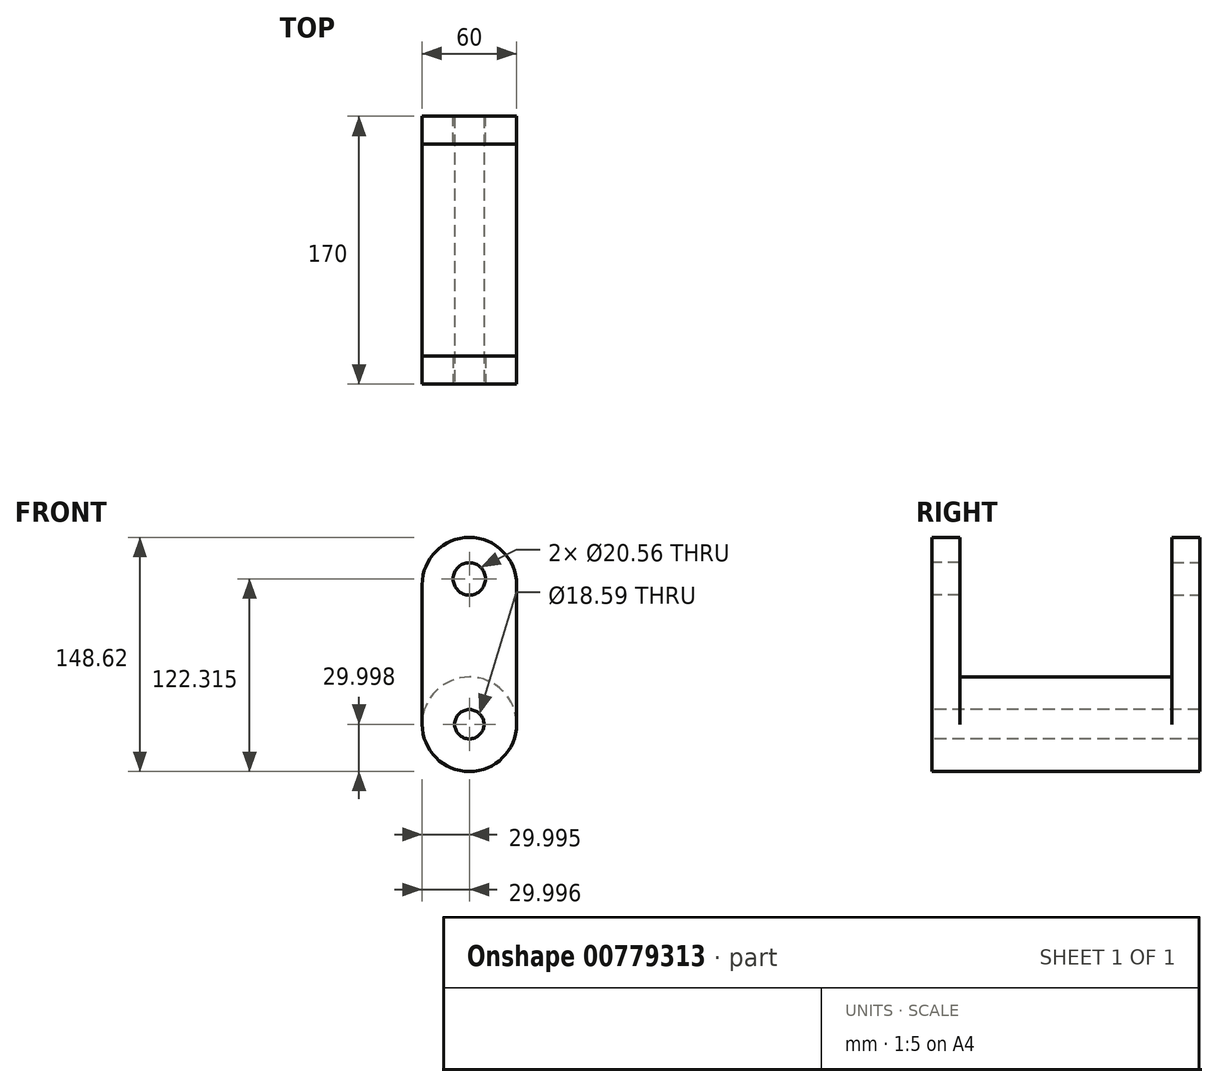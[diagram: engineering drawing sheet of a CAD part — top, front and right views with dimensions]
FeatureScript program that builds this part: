
annotation { "Feature Type Name" : "Feature", "Feature Type Description" : "" }
export const myFeature = defineFeature(function(context is Context, id is Id, definition is map)
    precondition{}
    {
        {
            var Q0;
            Q0=qCreatedBy(makeId("Front.planeOp"),FACE);
            var sketch = newSketch(context, id + "F0", { "sketchPlane" : qUnion([Q0])});
            skLineSegment(sketch, "E0.left", {"start": v(-34.78, 40.1) * mm, "end": v(-34.78, -48.52) * mm});
            skLineSegment(sketch, "E0.right", {"start": v(25.22, 40.1) * mm, "end": v(25.22, -48.52) * mm});
            skArc(sketch, "E1", {"start": v(25.22, 40.1) * mm, "mid": v(-4.78, 70.1) * mm, "end": v(-34.78, 40.1) * mm});
            skCircle(sketch, "E2", {"center": v(-4.78, -48.52) * mm, "radius": 30 * mm});
            skPoint(sketch, "E2.centerSnap0", {"position": v(-4.78, -53.96) * mm});
            skPoint(sketch, "E3.orphan", {"position": v(-34.78, -53.96) * mm});
            skPoint(sketch, "E4.orphan", {"position": v(25.22, -53.96) * mm});
            skCircle(sketch, "E5", {"center": v(-4.78, 43.8) * mm, "radius": 10.28 * mm});
            skCircle(sketch, "E6", {"center": v(-4.78, -48.52) * mm, "radius": 9.3 * mm});
            skSolve(sketch);
        }
        {
            var Q0;
            Q0=makeQuery(id+"F0.imprint","IMPRINT",FACE,{"disambiguationData":[TD([[makeQuery(id+"F0.imprint","IMPRINT",EDGE,{"derivedFrom":sQuery(id+"F0.wireOp",EDGE,"E6")}),-1.0]])]});
            extrude(context, id + "F1", {"entities" : qUnion([Q0]), "oppositeDirection" : true, "depth" : 85 * mm, "offsetDistance" : 25 * mm});
        }
        {
            var Q0;
            Q0 = qSketchRegion(id + "F0", true);
            extrude(context, id + "F2", {"entities" : qUnion([Q0]), "operationType" : NewBodyOperationType.ADD, "oppositeDirection" : true, "depth" : 17.7 * mm, "offsetDistance" : 25 * mm});
        }
        {
            var Q0;
            Q0=qCreatedBy(makeId("Front.planeOp"),FACE);
            cPlane(context, id + "F3", {"entities" : qUnion([Q0]), "cplaneType" : CPlaneType.OFFSET, "offset" : 85 * mm, "oppositeDirection" : true, "width" : 150 * mm, "height" : 150 * mm});
        }
        {
            var Q0;
            Q0=makeQuery(id+"F1.opExtrude","SWEPT_BODY",BODY,{"disambiguationData":[OSD([sQuery(id+"F0.wireOp",EDGE,"E2"),sQuery(id+"F0.wireOp",EDGE,"E6")])]});
            var Q1;
            Q1=qCreatedBy(id+"F3.planeOp",FACE);
            mirror(context, id + "F4", {"operationType" : NewBodyOperationType.ADD, "entities" : qUnion([Q0]), "mirrorPlane" : qUnion([Q1])});
        }
    });
